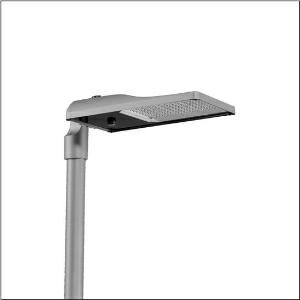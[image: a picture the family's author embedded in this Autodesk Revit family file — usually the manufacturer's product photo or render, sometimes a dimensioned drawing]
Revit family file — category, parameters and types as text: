
# Revit family: streetlight_sl_31_maxi___st0_5a_5xh8b31t08ta_8beb
name_source: partatom
category: Lighting Fixtures
units: mm (PartAtom-declared; Revit-internal decimal feet)

## family parameters
Cut with Voids When Loaded = No
Host = Face
Light Source = No
Part Type = Normal
Room Calculation Point = No
Round Connector Dimension = Use Diameter
Shared = No

## types (1)
- --- (1 x LED, 33650 lm, 228.8 W, 3000K)
    Apparent Load = 229 VA
    CIE Flux Codes = 43 76 97 100 100
    Color Rendering = 70
    Color Temperature = 3000K
    Default Elevation = 1800 mm
    Description = Streetlight SL 31 maxi, mast luminaire, primary light control with lens, of PMMA, primary optical cover: cover, of toughened safety glass, transparent, light distribution: ST0.5a, light emission: direct distribution, primary light characteristic: asymmetric, installation type: post-top, side-entry, LED, High Power LED, rated luminous flux: 33.650lm, luminous efficacy: 147lm/W, light colour: 730, colour temperature: 3000K, control: presetting dimming logarithmic, flexible luminous flux parameterisation, time-dependent luminous flux control, constant luminous flux control, power reduction, intelligent temperature release in ECG and LED module, overheat protection, with cable H07RN-F 2x 1.5mm², mains connection: 220..240V, AC, 50/60Hz, connection cable pre-assembled, cable length: 14,5m, start of lifetime: 229W, end of service life: 249W, reduction: 102W, luminaire housing, of diecast aluminium, powder-coated, Siteco® metallic grey (DB 702S), corrosivity category C5 high according to DIN EN ISO 12944, sealing non-destructively replaceable, multi-level sealing system, mast flange (76/60mm) included as standard, inclination: -15°..+20° (post-top) | -20°..+20° (side-entry), adjustable in 5° steps, no sealing on luminaire upper side, Smart Interface below and above, protection rating (complete): IP66, insulation class (complete): insulation class II (safety insulation), certification: CE, ENEC, ENEC+, VDE, UKCA, ZD4i, impact resistance: IK09, permissible operating ambient temperature for outdoor applications: -40..+50°C, standard-compliant lighting for roads and squares, packaging unit: 1 piece

Light Distribution: ST0.5a
    Height = 79 mm
    Lamp = 1 x LED
    Lamp Light Flux = 33650 lm
    Lamp Power = 228.8 W
    Lamp count = 1
    Length = 657 mm
    Luminous efficacy = 147 lm/W
    Manufacturer = Siteco
    ModVariant = No
    Model = 5XH8B31T08TA
    Number of Poles = 1
    OnlyDefault = Yes
    Power Factor = 1
    Product Name = Streetlight SL 31 maxi | ST0.5a
    Product group = mast luminaire | pylon top
    ProductGroupID = 6100
    Protection Class = Protection class II
    Protection Degree = IP 66
    RLX_Detail_Level = 1
    RLX_Emergency_Light_Flux = 0 lm
    RLX_Emergency_Type = 0
    RLX_Emergency_Type_DB = No
    RlxData = <blob elided: 58753 chars, md5=22a9d1ff>
    Socket = socket
    Standby Power = 0 W
    System Light Flux = 33650 lm
    System Power = 229 W
    Type Comments = factory setting: luminous flux: 100 % | dim-lin: 254 | 802 mA
    Type Image = l_1300303.jpg
    URL = http://relux.com
    VarID = @adj_002459
    Voltage = 0 V
    Weight = 0.00 kg
    Width = 362 mm

## geometry (parser evidence)
native form markers: Blend x4, Sweep x12
no freeform markers — native parametric forms only
